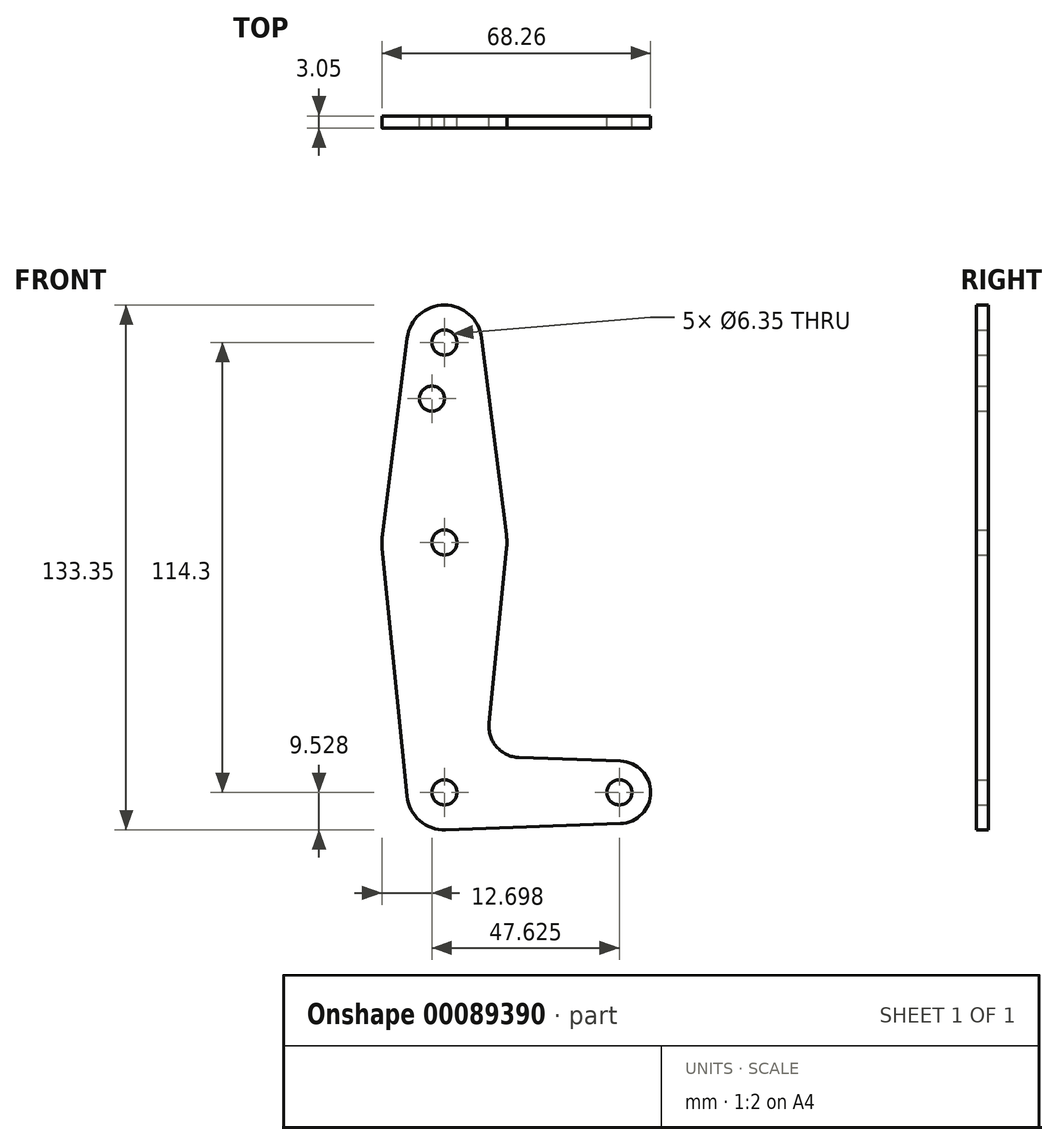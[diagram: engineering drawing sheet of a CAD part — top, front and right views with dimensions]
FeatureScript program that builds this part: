
annotation { "Feature Type Name" : "Feature", "Feature Type Description" : "" }
export const myFeature = defineFeature(function(context is Context, id is Id, definition is map)
    precondition{}
    {
        {
            var Q0;
            Q0=qCreatedBy(makeId("Front.planeOp"),FACE);
            var sketch = newSketch(context, id + "F0", { "sketchPlane" : qUnion([Q0])});
            skCircle(sketch, "E0", {"center": v(-56.66, 58.19) * mm, "radius": 9.53 * mm});
            skCircle(sketch, "E1", {"center": v(-56.66, 7.39) * mm, "radius": 15.87 * mm});
            skCircle(sketch, "E2", {"center": v(-56.66, -56.11) * mm, "radius": 9.53 * mm});
            skCircle(sketch, "E3", {"center": v(-12.2, -56.11) * mm, "radius": 7.94 * mm});
            skLineSegment(sketch, "E4", {"start": v(-66.1, 59.38) * mm, "end": v(-72.4, 9.37) * mm});
            skLineSegment(sketch, "E5", {"start": v(-47.2, 59.38) * mm, "end": v(-40.9, 9.37) * mm});
            skLineSegment(sketch, "E6", {"start": v(-66.13, -57.06) * mm, "end": v(-72.45, 5.8) * mm});
            skLineSegment(sketch, "E7", {"start": v(-45.32, -38.52) * mm, "end": v(-40.86, 5.8) * mm});
            skLineSegment(sketch, "E8", {"start": v(-37.69, -47.26) * mm, "end": v(-11.92, -48.18) * mm});
            skLineSegment(sketch, "E9", {"start": v(-56.32, -65.63) * mm, "end": v(-11.92, -64.04) * mm});
            skCircle(sketch, "E10", {"center": v(-59.83, 43.91) * mm, "radius": 3.18 * mm});
            skCircle(sketch, "E11", {"center": v(-56.66, 58.19) * mm, "radius": 3.18 * mm});
            skCircle(sketch, "E12", {"center": v(-56.66, 7.39) * mm, "radius": 3.18 * mm});
            skCircle(sketch, "E13", {"center": v(-56.66, -56.11) * mm, "radius": 3.18 * mm});
            skCircle(sketch, "E14", {"center": v(-12.2, -56.11) * mm, "radius": 3.18 * mm});
            skLineSegment(sketch, "E15", {"start": v(-56.66, 58.19) * mm, "end": v(-56.66, -56.11) * mm, "construction": true});
            skLineSegment(sketch, "E16", {"start": v(-56.66, -56.11) * mm, "end": v(-12.2, -56.11) * mm, "construction": true});
            skArc(sketch, "E17.filletArc", {"start": v(-45.32, -38.52) * mm, "mid": v(-43.4, -44.54) * mm, "end": v(-37.69, -47.26) * mm});
            skSolve(sketch);
        }
        {
            var Q0;
            Q0 = qSketchRegion(id + "F0", true);
            extrude(context, id + "F1", {"entities" : qUnion([Q0]), "depth" : 3.05 * mm});
        }
    });
